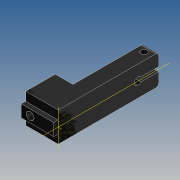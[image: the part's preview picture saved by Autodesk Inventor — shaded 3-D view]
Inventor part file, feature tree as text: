
AUTODESK INVENTOR PART (.ipt)
format: ipt  version: 2017 (Build 210142000, 142)  size: 258,560 bytes
history: native  units: mm
features: sketch x7, hole x4, extrude x3, fillet x2, mirror x1
ambient origin geometry x8: Origin, YZ Plane, XZ Plane, XY Plane, X Axis, Y Axis, Z Axis, Center Point
bodies: Solid1 (feature_tree)
feature tree (17):
  extrude  "Extrusion1"  Depth=10.0mm
  extrude  "Extrusion2"  Depth=20.0mm
  hole  "Hole2"  [1 undecoded]
  hole  "Perçage3"  [1 undecoded]
  fillet  "Congé2"  Radius=16.0mm
  fillet  "Congé3"  Radius=54.0mm
  hole  "Perçage4"  [1 undecoded]
  extrude  "Extrusion3"  Depth=2.0mm
  mirror  "Symétrie1"
  hole  "Perçage5"  [1 undecoded]
  sketch  "Sketch1"  dims[d0=68.0mm d1=10.0mm]
  sketch  "Sketch2"  dims[d2=22.0mm d3=20.0mm]
  sketch  "Sketch4"  dims[d4=20.0mm d5=0.0mm d6=8.2mm d7=3.0mm d8=0.0mm d18=16.0mm d19=5.3mm d20=6.0mm d21=10.0mm d22=6.0mm d23=90.0deg d24=8.0mm d25=20.594885mm d28=54.0mm d29=5.0mm d30=6.0mm d31=4.0mm d32=2.0mm d33=90.0deg d34=8.0mm d35=20.594885mm d36=2.0mm d37=2.0mm d38=54.0mm d39=10.5mm d40=6.0mm d41=4.0mm d42=2.0mm d43=90.0deg d44=6.0mm d45=0.0mm d50=54.0mm d51=3.0mm d52=10.0mm d53=16.803301mm d54=8.939608mm d55=93.232253mm d56=10.0mm d57=0.0mm d58=5.0mm d59=63.0mm d60=4.2mm d61=6.0mm d62=4.0mm d63=2.0mm d64=90.0deg d65=10.0mm d66=0.0mm]
  sketch  "Esquisse5"
  sketch  "Esquisse6"
  sketch  "Esquisse8"
  sketch  "Esquisse9"
note: 4 required parameter values undecoded (feature->parameter linkage not recoverable at this tier; creation-order binding heuristic only, values carry confidence <= 0.55)
